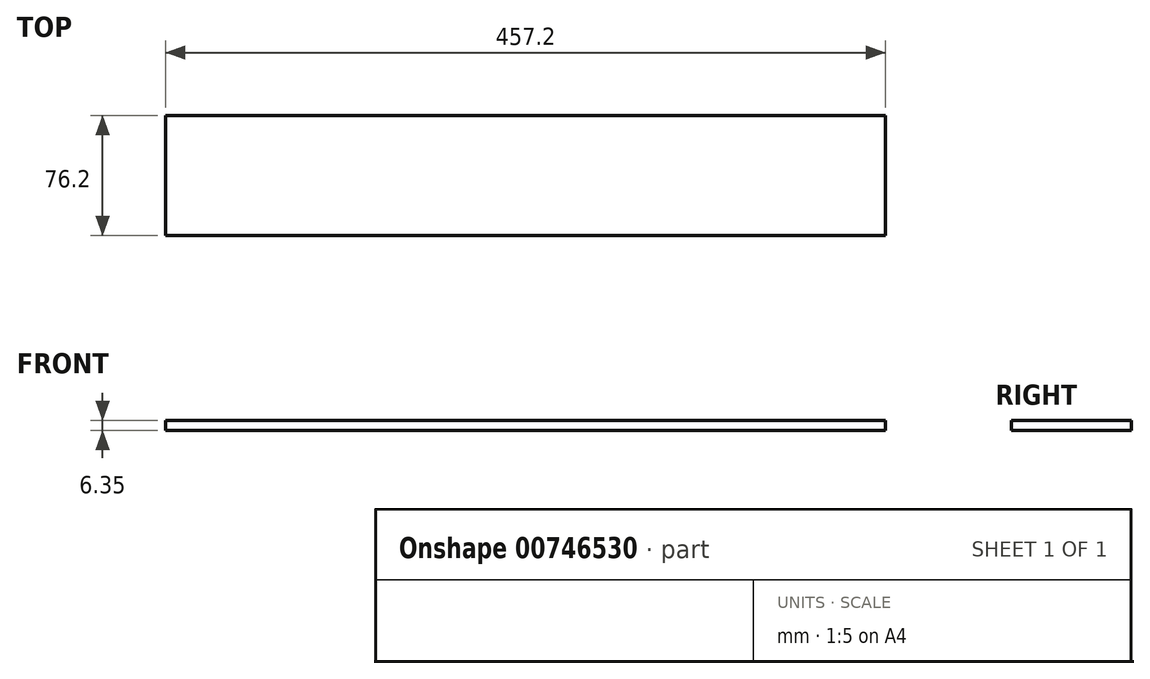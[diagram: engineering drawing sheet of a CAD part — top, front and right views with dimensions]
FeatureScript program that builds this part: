
annotation { "Feature Type Name" : "Feature", "Feature Type Description" : "" }
export const myFeature = defineFeature(function(context is Context, id is Id, definition is map)
    precondition{}
    {
        {
            var Q0;
            Q0=qCreatedBy(makeId("Top.planeOp"),FACE);
            var sketch = newSketch(context, id + "F0", { "sketchPlane" : qUnion([Q0])});
            skLineSegment(sketch, "E0.bottom", {"start": v(-242.09, -113.43) * mm, "end": v(215.11, -113.43) * mm});
            skLineSegment(sketch, "E0.top", {"start": v(-242.09, -189.63) * mm, "end": v(215.11, -189.63) * mm});
            skLineSegment(sketch, "E0.left", {"start": v(-242.09, -113.43) * mm, "end": v(-242.09, -189.63) * mm});
            skLineSegment(sketch, "E0.right", {"start": v(215.11, -113.43) * mm, "end": v(215.11, -189.63) * mm});
            skSolve(sketch);
        }
        {
            var Q0;
            Q0=makeQuery(id+"F0.imprint","IMPRINT",FACE,{"disambiguationData":[TD([[makeQuery(id+"F0.imprint","IMPRINT",EDGE,{"derivedFrom":sQuery(id+"F0.wireOp",EDGE,"E0.bottom")}),-1.0]])]});
            var sketch = newSketch(context, id + "F1", { "sketchPlane" : qUnion([Q0])});
            skSolve(sketch);
        }
        {
            var Q0;
            Q0=makeQuery(id+"F1.imprint","IMPRINT",FACE,{"disambiguationData":[TD([[makeQuery(id+"F1.imprint","IMPRINT",EDGE,{"derivedFrom":makeQuery(id+"F0.imprint","IMPRINT",EDGE,{"derivedFrom":sQuery(id+"F0.wireOp",EDGE,"E0.bottom")})}),-1.0]])]});
            extrude(context, id + "F2", {"entities" : qUnion([Q0]), "depth" : 6.35 * mm, "offsetDistance" : 25.4 * mm});
        }
    });
